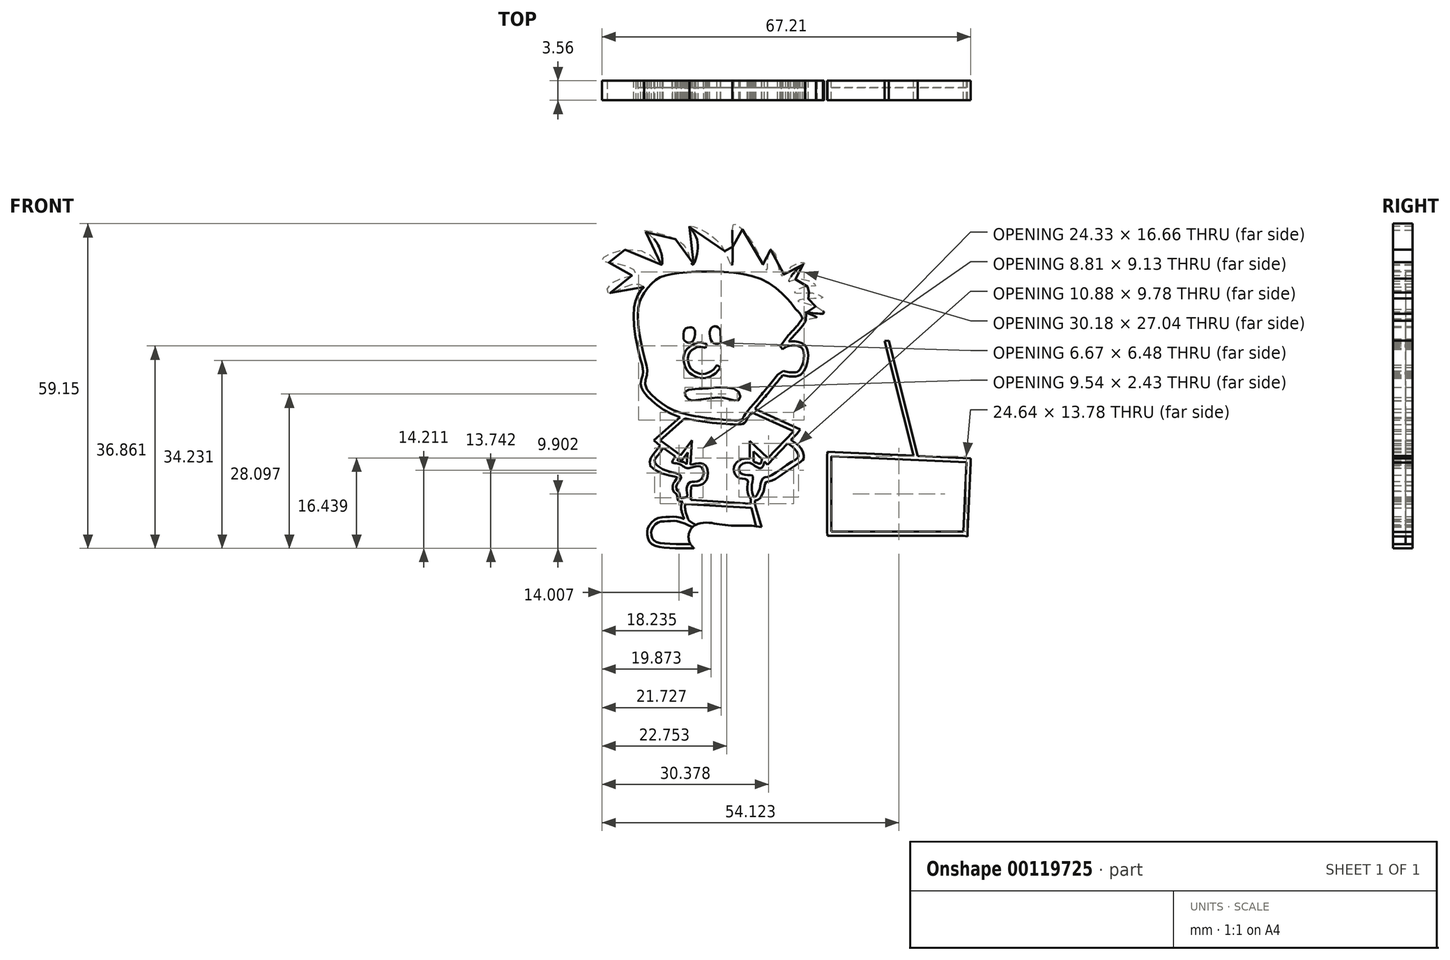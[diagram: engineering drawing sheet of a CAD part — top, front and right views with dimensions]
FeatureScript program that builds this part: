
annotation { "Feature Type Name" : "Feature", "Feature Type Description" : "" }
export const myFeature = defineFeature(function(context is Context, id is Id, definition is map)
    precondition{}
    {
        {
            var Q0;
            Q0=qCreatedBy(makeId("Front.planeOp"),FACE);
            var sketch = newSketch(context, id + "F0", { "sketchPlane" : qUnion([Q0])});
            skLineSegment(sketch, "E0.bottom", {"start": v(118.99, 18.23) * mm, "end": v(195.19, 18.23) * mm});
            skLineSegment(sketch, "E0.top", {"start": v(118.99, -45.27) * mm, "end": v(195.19, -45.27) * mm});
            skLineSegment(sketch, "E0.left", {"start": v(118.99, 18.23) * mm, "end": v(118.99, -45.27) * mm});
            skLineSegment(sketch, "E0.right", {"start": v(195.19, 18.23) * mm, "end": v(195.19, -45.27) * mm});
            skFitSpline(sketch, "E1", {"points": [v(128.75, 4.52) * mm, v(127.83, 2.6) * mm, v(127.76, -2.24) * mm, v(128.83, -7.5) * mm, v(129.18, -8.7) * mm, v(129.25, -10.42) * mm, v(128.9, -12.2) * mm, v(130.67, -14.61) * mm, v(133.8, -16.74) * mm, v(139.35, -18.17) * mm, v(146.53, -18.6) * mm, v(146.74, -18.24) * mm, v(148.73, -15.68) * mm, v(153.07, -10.42) * mm], "startDerivative": vector(-17.26, -27.17) * mm, "endDerivative": vector(40.4, 49.7) * mm});
            skFitSpline(sketch, "E2", {"points": [v(153.92, -10.49) * mm, v(156.84, -10.63) * mm, v(158.05, -9.35) * mm, v(158.62, -7.29) * mm, v(157.9, -4.94) * mm, v(155.06, -4.37) * mm, v(153.5, -5.15) * mm], "startDerivative": vector(17.4, -3.35) * mm, "endDerivative": vector(-9.1, -6.67) * mm});
            skFitSpline(sketch, "E3", {"points": [v(128.75, 5.58) * mm, v(126.4, 6) * mm, v(122.14, 4.52) * mm, v(122.92, 6.36) * mm, v(127.19, 8.07) * mm, v(125.2, 9.5) * mm, v(121.07, 10.42) * mm, v(122.78, 11.77) * mm, v(129.47, 11.63) * mm, v(131.88, 9.64) * mm, v(130.96, 13.76) * mm, v(128.75, 15.82) * mm, v(132.52, 15.04) * mm, v(136.58, 12.27) * mm, v(137.57, 9.64) * mm, v(138.35, 14.26) * mm, v(137, 16.6) * mm, v(142.12, 13.9) * mm, v(144.68, 9.5) * mm, v(144.82, 13.83) * mm, v(145.18, 17.1) * mm, v(147.45, 15.04) * mm, v(149.8, 11.06) * mm, v(151.15, 8.57) * mm, v(151.5, 12.2) * mm, v(152.5, 11.84) * mm, v(153.71, 7.64) * mm, v(155.92, 9.56) * mm, v(158.05, 10) * mm, v(157.05, 9.2) * mm, v(155.06, 6.65) * mm, v(157.05, 7.08) * mm, v(160.04, 5.87) * mm, v(157.76, 5.51) * mm, v(156.13, 4.52) * mm, v(159.12, 4.52) * mm, v(161.32, 3.6) * mm, v(158.55, 3.45) * mm, v(156.7, 3.02) * mm, v(159.47, 2.24) * mm, v(161.4, 0.75) * mm, v(158.2, 0.96) * mm, v(160.18, 0.04) * mm, v(159.4, -0.18) * mm, v(158.2, -0.6) * mm], "startDerivative": vector(-96.12, 50.27) * mm, "endDerivative": vector(-71.57, -34.9) * mm});
            skFitSpline(sketch, "E4", {"points": [v(155.06, -4.37) * mm, v(155.99, -3.3) * mm, v(157.27, -1.88) * mm, v(158.2, -0.6) * mm], "startDerivative": vector(2.8, 3.3) * mm, "endDerivative": vector(2.6, 3.86) * mm});
            skFitSpline(sketch, "E5", {"points": [v(137.88, -2.14) * mm, v(137.17, -1.78) * mm, v(136.15, -2.14) * mm, v(135.91, -3.15) * mm, v(135.97, -4) * mm, v(136.87, -4.6) * mm, v(137.64, -4.23) * mm, v(138.02, -2.92) * mm, v(137.88, -2.14) * mm]});
            skFitSpline(sketch, "E6", {"points": [v(142.49, -2.02) * mm, v(141.41, -1.6) * mm, v(140.75, -2.26) * mm, v(140.75, -3.63) * mm, v(141.35, -4.65) * mm, v(142.55, -4.59) * mm, v(142.67, -3.33) * mm, v(142.49, -2.02) * mm]});
            skFitSpline(sketch, "E7", {"points": [v(139.92, -5.55) * mm, v(138.9, -5.3) * mm, v(138.02, -5.57) * mm, v(136.8, -6.74) * mm, v(137.1, -9.07) * mm, v(138.02, -9.85) * mm, v(139.26, -10.27) * mm, v(140.93, -9.8) * mm, v(142.01, -8.66) * mm], "startDerivative": vector(-9.98, 3.85) * mm, "endDerivative": vector(7.15, 9.6) * mm});
            skLineSegment(sketch, "E8", {"start": v(136.3, -18.24) * mm, "end": v(131.64, -22.37) * mm});
            skLineSegment(sketch, "E9", {"start": v(148.14, -17.16) * mm, "end": v(155.97, -20.7) * mm});
            skLineSegment(sketch, "E10", {"start": v(155.97, -20.7) * mm, "end": v(150.65, -26.25) * mm});
            skLineSegment(sketch, "E11", {"start": v(150.65, -26.25) * mm, "end": v(148.7, -24.38) * mm});
            skLineSegment(sketch, "E12", {"start": v(148.7, -24.38) * mm, "end": v(148.7, -26.85) * mm});
            skFitSpline(sketch, "E13", {"points": [v(132.03, -24) * mm, v(131.28, -25.06) * mm, v(130.62, -26.17) * mm, v(131.83, -27.47) * mm, v(133.8, -28.18) * mm, v(135.4, -28.83) * mm, v(135.15, -29.79) * mm, v(134.54, -30.9) * mm, v(134.85, -31.6) * mm, v(134.95, -31.6) * mm], "startDerivative": vector(-5.75, -8.92) * mm, "endDerivative": vector(2.74, 1.08) * mm});
            skFitSpline(sketch, "E14", {"points": [v(136.05, -32.8) * mm, v(136.56, -32.6) * mm, v(136.5, -31.6) * mm, v(136.6, -30.7) * mm, v(137.1, -29.99) * mm, v(138.32, -29.89) * mm, v(139.42, -28.98) * mm, v(139.37, -27.52) * mm, v(138.57, -27.07) * mm, v(136.86, -27.42) * mm, v(136.05, -27.22) * mm, v(134.95, -26.62) * mm, v(133.84, -26.37) * mm, v(134.34, -25.41) * mm, v(134.44, -25.06) * mm], "startDerivative": vector(12.12, 1.45) * mm, "endDerivative": vector(0.3, 6.69) * mm});
            skFitSpline(sketch, "E15", {"points": [v(136.05, -32.8) * mm, v(135.35, -32.8) * mm, v(135.2, -32.2) * mm, v(134.95, -31.6) * mm], "startDerivative": vector(-2.5, -0.51) * mm, "endDerivative": vector(-0.94, 1.68) * mm});
            skLineSegment(sketch, "E16", {"start": v(131.64, -22.37) * mm, "end": v(135.42, -25.1) * mm});
            skLineSegment(sketch, "E17", {"start": v(135.42, -25.1) * mm, "end": v(137.4, -22.33) * mm});
            skLineSegment(sketch, "E18", {"start": v(137.4, -22.33) * mm, "end": v(137.14, -27.38) * mm});
            skPoint(sketch, "E19.1.internal.snap0", {"position": v(153.3, -23.47) * mm});
            skFitSpline(sketch, "E19", {"points": [v(154.73, -22.86) * mm, v(155.69, -23.47) * mm, v(156.6, -24.51) * mm, v(156.86, -25.31) * mm, v(155.48, -26.38) * mm, v(151.37, -28.99) * mm, v(150.41, -29.26) * mm, v(149.94, -30.43) * mm, v(149.72, -31.39) * mm, v(148.92, -32.72) * mm, v(148.44, -32.08) * mm, v(148.4, -30.32) * mm, v(148.5, -28.83) * mm, v(147.22, -28.67) * mm, v(146.05, -28.03) * mm, v(146.31, -26.91) * mm, v(147.75, -26.43) * mm, v(148.7, -26.85) * mm], "startDerivative": vector(18.4, -9.84) * mm, "endDerivative": vector(16.58, -11.15) * mm});
            skFitSpline(sketch, "E20", {"points": [v(148.7, -26.85) * mm, v(150.04, -27.44) * mm, v(150.65, -26.25) * mm], "startDerivative": vector(3, -2.09) * mm, "endDerivative": vector(0.9, 3.33) * mm});
            skFitSpline(sketch, "E21", {"points": [v(137.1, -37.14) * mm, v(134.8, -36.34) * mm, v(133, -36.34) * mm, v(130.92, -36.66) * mm, v(129.53, -38.1) * mm, v(129.27, -39.43) * mm, v(129.9, -41.08) * mm, v(132.04, -41.88) * mm, v(136.56, -42.04) * mm], "startDerivative": vector(-18.13, 7.82) * mm, "endDerivative": vector(27.1, 0) * mm});
            skFitSpline(sketch, "E22", {"points": [v(145.83, -37.94) * mm, v(142.8, -37.73) * mm, v(140.32, -37.37) * mm, v(137.9, -37.88) * mm, v(136.88, -39.38) * mm, v(137, -40.87) * mm, v(138.16, -42.3) * mm, v(141.04, -43.58) * mm, v(144.05, -43.85) * mm, v(147.49, -43.8) * mm, v(151.59, -43.8) * mm, v(153.3, -43.32) * mm, v(154.4, -41.88) * mm, v(154.1, -40.5) * mm, v(153.02, -39.06) * mm, v(151.53, -38.42) * mm, v(149.62, -38.1) * mm, v(147.97, -37.9) * mm, v(145.83, -37.94) * mm]});
            skFitSpline(sketch, "E23", {"points": [v(136.56, -42.04) * mm, v(137.84, -42.04) * mm], "startDerivative": vector(1.28, 0) * mm, "endDerivative": vector(1.28, 0) * mm});
            skFitSpline(sketch, "E24", {"points": [v(137.1, -37.14) * mm, v(137.52, -37.41) * mm, v(138.1, -37.77) * mm], "startDerivative": vector(0.86, -0.58) * mm, "endDerivative": vector(1.12, -0.67) * mm});
            skLineSegment(sketch, "E25", {"start": v(187.5, -26.36) * mm, "end": v(162.86, -25.25) * mm});
            skLineSegment(sketch, "E26", {"start": v(162.86, -25.25) * mm, "end": v(162.86, -39.03) * mm});
            skLineSegment(sketch, "E27", {"start": v(162.86, -39.03) * mm, "end": v(186.89, -39.03) * mm});
            skLineSegment(sketch, "E28", {"start": v(186.89, -39.03) * mm, "end": v(187.5, -26.36) * mm});
            skLineSegment(sketch, "E29", {"start": v(178.75, -25.82) * mm, "end": v(173.3, -4.2) * mm});
            skLineSegment(sketch, "E30", {"start": v(177.9, -25.59) * mm, "end": v(172.52, -4.23) * mm});
            skLineSegment(sketch, "E31", {"start": v(172.52, -4.23) * mm, "end": v(173.3, -4.2) * mm});
            skLineSegment(sketch, "E32", {"start": v(177.9, -25.59) * mm, "end": v(178, -25.93) * mm});
            skLineSegment(sketch, "E33", {"start": v(178.75, -25.82) * mm, "end": v(178.8, -25.97) * mm});
            skLineSegment(sketch, "E34.0", {"start": v(162.1, -25.25) * mm, "end": v(162.1, -39.03) * mm});
            skLineSegment(sketch, "E35.0", {"start": v(187.53, -25.6) * mm, "end": v(162.89, -24.49) * mm});
            skLineSegment(sketch, "E36.0", {"start": v(187.65, -39.06) * mm, "end": v(188.25, -26.4) * mm});
            skLineSegment(sketch, "E37.0", {"start": v(162.86, -39.79) * mm, "end": v(186.89, -39.79) * mm});
            skLineSegment(sketch, "E38", {"start": v(162.86, -39.79) * mm, "end": v(162.13, -39.79) * mm});
            skLineSegment(sketch, "E39", {"start": v(162.13, -39.79) * mm, "end": v(162.1, -39.03) * mm});
            skLineSegment(sketch, "E40", {"start": v(162.89, -24.49) * mm, "end": v(162.13, -24.45) * mm});
            skLineSegment(sketch, "E41", {"start": v(162.13, -24.45) * mm, "end": v(162.1, -25.25) * mm});
            skLineSegment(sketch, "E42", {"start": v(187.53, -25.6) * mm, "end": v(188.26, -25.63) * mm});
            skLineSegment(sketch, "E43", {"start": v(188.26, -25.63) * mm, "end": v(188.25, -26.4) * mm});
            skFitSpline(sketch, "E44", {"points": [v(136.36, -33.2) * mm, v(135.94, -33.42) * mm, v(135.67, -33.7) * mm, v(135.47, -34.19) * mm, v(135.46, -34.8) * mm, v(135.65, -35.6) * mm, v(135.87, -36.25) * mm, v(136.04, -36.7) * mm], "startDerivative": vector(-3.4, -1.64) * mm, "endDerivative": vector(1.3, -3.3) * mm});
            skLineSegment(sketch, "E45", {"start": v(148.92, -32.72) * mm, "end": v(148.92, -33.98) * mm});
            skLineSegment(sketch, "E46", {"start": v(148.92, -33.98) * mm, "end": v(136.36, -33.2) * mm});
            skFitSpline(sketch, "E47", {"points": [v(148.92, -33.98) * mm, v(150.1, -38.17) * mm], "startDerivative": vector(1.18, -4.2) * mm, "endDerivative": vector(1.18, -4.2) * mm});
            skLineSegment(sketch, "E48", {"start": v(136.56, -32.6) * mm, "end": v(136.56, -33.2) * mm});
            skLineSegment(sketch, "E49", {"start": v(187.65, -39.06) * mm, "end": v(187.65, -39.86) * mm});
            skLineSegment(sketch, "E50", {"start": v(187.65, -39.86) * mm, "end": v(186.89, -39.79) * mm});
            skLineSegment(sketch, "E51", {"start": v(132.03, -24) * mm, "end": v(132.67, -23.11) * mm});
            skLineSegment(sketch, "E52", {"start": v(132.67, -23.11) * mm, "end": v(132.74, -23.2) * mm});
            skLineSegment(sketch, "E53", {"start": v(134.44, -25.06) * mm, "end": v(134.76, -24.62) * mm});
            skLineSegment(sketch, "E54", {"start": v(134.76, -24.62) * mm, "end": v(134.66, -24.52) * mm});
            skLineSegment(sketch, "E55", {"start": v(136.3, -18.24) * mm, "end": v(136.87, -17.73) * mm});
            skLineSegment(sketch, "E56", {"start": v(148.14, -17.16) * mm, "end": v(147.66, -16.95) * mm});
            skLineSegment(sketch, "E57", {"start": v(154.73, -22.86) * mm, "end": v(154.2, -22.53) * mm});
            skLineSegment(sketch, "E58", {"start": v(128.75, 4.52) * mm, "end": v(128.75, 5.58) * mm});
            skFitSpline(sketch, "E59.0", {"points": [v(128.11, 4.92) * mm, v(127.93, 4.64) * mm, v(127.64, 4.18) * mm, v(127.3, 3.43) * mm, v(127.08, 2.78) * mm, v(126.93, 2.05) * mm, v(126.82, 1) * mm, v(126.81, -0.46) * mm, v(126.98, -2.38) * mm, v(127.3, -4.38) * mm, v(127.63, -5.91) * mm, v(127.88, -6.95) * mm, v(128.03, -7.5) * mm, v(128.14, -7.86) * mm, v(128.23, -8.17) * mm, v(128.33, -8.47) * mm, v(128.4, -8.73) * mm, v(128.45, -8.95) * mm, v(128.5, -9.2) * mm, v(128.54, -9.47) * mm, v(128.55, -9.75) * mm, v(128.54, -9.95) * mm, v(128.53, -10.15) * mm, v(128.5, -10.33) * mm, v(128.44, -10.53) * mm, v(128.35, -10.83) * mm, v(128.23, -11.17) * mm, v(128.14, -11.59) * mm, v(128.12, -11.88) * mm, v(128.12, -12.12) * mm, v(128.14, -12.31) * mm, v(128.18, -12.5) * mm, v(128.25, -12.75) * mm, v(128.37, -13.04) * mm, v(128.6, -13.47) * mm, v(128.97, -13.98) * mm, v(129.5, -14.55) * mm, v(130.05, -15.08) * mm, v(130.62, -15.58) * mm, v(131.21, -16.05) * mm, v(132.03, -16.64) * mm, v(133.12, -17.3) * mm, v(134.56, -17.92) * mm, v(135.92, -18.3) * mm, v(137.15, -18.58) * mm, v(138.15, -18.76) * mm, v(139.25, -18.92) * mm, v(140.45, -19.09) * mm, v(141.7, -19.23) * mm, v(142.95, -19.35) * mm, v(143.92, -19.42) * mm, v(144.63, -19.46) * mm, v(145.13, -19.47) * mm, v(145.58, -19.47) * mm, v(145.98, -19.46) * mm, v(146.27, -19.43) * mm, v(146.5, -19.4) * mm, v(146.65, -19.36) * mm, v(146.83, -19.3) * mm, v(147.03, -19.2) * mm, v(147.21, -19.03) * mm, v(147.34, -18.83) * mm, v(147.4, -18.68) * mm, v(147.43, -18.59) * mm, v(147.44, -18.54) * mm, v(147.45, -18.52) * mm, v(147.45, -18.51) * mm, v(147.46, -18.5) * mm, v(147.48, -18.45) * mm, v(147.52, -18.39) * mm, v(147.59, -18.28) * mm, v(147.7, -18.12) * mm, v(147.87, -17.9) * mm, v(148.07, -17.65) * mm, v(148.37, -17.28) * mm, v(148.8, -16.78) * mm, v(149.37, -16.11) * mm, v(149.95, -15.42) * mm, v(150.55, -14.7) * mm, v(151.36, -13.72) * mm, v(152.4, -12.45) * mm, v(153.24, -11.41) * mm, v(153.66, -10.9) * mm]});
            skFitSpline(sketch, "E60", {"points": [v(153.07, -10.42) * mm, v(153.36, -10.48) * mm, v(153.59, -10.5) * mm, v(153.92, -10.49) * mm], "startDerivative": vector(0.88, -0.23) * mm, "endDerivative": vector(0.98, 0.06) * mm});
            skFitSpline(sketch, "E61", {"points": [v(153.66, -10.9) * mm, v(153.92, -10.49) * mm], "startDerivative": vector(0.26, 0.4) * mm, "endDerivative": vector(0.26, 0.4) * mm});
            skFitSpline(sketch, "E62", {"points": [v(128.11, 4.92) * mm, v(128.75, 5.58) * mm], "startDerivative": vector(0.64, 0.66) * mm, "endDerivative": vector(0.64, 0.66) * mm});
            skFitSpline(sketch, "E63", {"points": [v(128.75, 4.52) * mm, v(130.9, 6.9) * mm, v(134.35, 8.04) * mm, v(141.92, 8.36) * mm, v(150.63, 6.74) * mm, v(155.23, 2.97) * mm, v(156.33, 1.55) * mm], "startDerivative": vector(14.38, 19.77) * mm, "endDerivative": vector(8.83, -12.25) * mm});
            skFitSpline(sketch, "E64.0", {"points": [v(154.48, -3.88) * mm, v(154.6, -3.74) * mm, v(154.83, -3.46) * mm, v(155.21, -3.02) * mm, v(155.65, -2.55) * mm, v(156.1, -2.06) * mm, v(156.54, -1.57) * mm, v(156.9, -1.11) * mm, v(157.24, -0.65) * mm, v(157.45, -0.34) * mm, v(157.56, -0.18) * mm]});
            skFitSpline(sketch, "E65", {"points": [v(156.33, 1.55) * mm, v(157.18, 0.63) * mm, v(157.56, -0.18) * mm], "startDerivative": vector(1.76, -1.68) * mm, "endDerivative": vector(0.66, -1.77) * mm});
            skFitSpline(sketch, "E66.0", {"points": [v(140.2, -4.84) * mm, v(140.08, -4.8) * mm, v(139.84, -4.7) * mm, v(139.47, -4.6) * mm, v(139.07, -4.54) * mm, v(138.63, -4.55) * mm, v(138.23, -4.64) * mm, v(137.87, -4.79) * mm, v(137.53, -4.96) * mm, v(137.14, -5.2) * mm, v(136.73, -5.51) * mm, v(136.4, -5.88) * mm, v(136.2, -6.23) * mm, v(136.06, -6.54) * mm, v(135.98, -6.85) * mm, v(135.93, -7.27) * mm, v(135.93, -7.8) * mm, v(136.03, -8.4) * mm, v(136.2, -8.96) * mm, v(136.44, -9.47) * mm, v(136.76, -9.9) * mm, v(137.12, -10.21) * mm, v(137.4, -10.4) * mm, v(137.62, -10.5) * mm, v(137.82, -10.6) * mm, v(138.1, -10.75) * mm, v(138.5, -10.9) * mm, v(138.98, -11.02) * mm, v(139.5, -11.05) * mm, v(140.01, -10.98) * mm, v(140.51, -10.85) * mm, v(140.9, -10.69) * mm, v(141.2, -10.52) * mm, v(141.5, -10.34) * mm, v(141.81, -10.08) * mm, v(142.23, -9.64) * mm, v(142.47, -9.31) * mm, v(142.62, -9.11) * mm]});
            skLineSegment(sketch, "E67", {"start": v(139.92, -5.55) * mm, "end": v(140.2, -4.84) * mm});
            skLineSegment(sketch, "E68", {"start": v(142.01, -8.66) * mm, "end": v(142.62, -9.11) * mm});
            skFitSpline(sketch, "E69.0", {"points": [v(154.07, -9.74) * mm, v(154.43, -9.8) * mm, v(154.96, -9.9) * mm, v(155.59, -9.99) * mm, v(156, -10) * mm, v(156.29, -9.99) * mm, v(156.46, -9.95) * mm, v(156.57, -9.92) * mm, v(156.66, -9.88) * mm, v(156.78, -9.8) * mm, v(156.92, -9.69) * mm, v(157.1, -9.48) * mm, v(157.26, -9.22) * mm, v(157.42, -8.9) * mm, v(157.6, -8.48) * mm, v(157.74, -8.04) * mm, v(157.83, -7.56) * mm, v(157.88, -7.05) * mm, v(157.86, -6.51) * mm, v(157.75, -6.06) * mm, v(157.63, -5.78) * mm, v(157.5, -5.6) * mm, v(157.38, -5.49) * mm, v(157.22, -5.38) * mm, v(156.96, -5.25) * mm, v(156.58, -5.13) * mm, v(156.15, -5.07) * mm, v(155.72, -5.06) * mm, v(155.32, -5.1) * mm, v(155, -5.16) * mm, v(154.73, -5.27) * mm, v(154.4, -5.45) * mm, v(154.14, -5.63) * mm, v(153.95, -5.77) * mm]});
            skLineSegment(sketch, "E70", {"start": v(153.5, -5.15) * mm, "end": v(153.95, -5.77) * mm});
            skLineSegment(sketch, "E71", {"start": v(153.07, -10.42) * mm, "end": v(154.07, -9.74) * mm});
            skLineSegment(sketch, "E72", {"start": v(154.48, -3.88) * mm, "end": v(153.7, -5) * mm});
            skLineSegment(sketch, "E73.0", {"start": v(135.8, -17.67) * mm, "end": v(131.13, -21.8) * mm});
            skLineSegment(sketch, "E74.0", {"start": v(131.2, -22.98) * mm, "end": v(134.98, -25.71) * mm});
            skFitSpline(sketch, "E75", {"points": [v(131.62, -23.3) * mm, v(130.74, -24.45) * mm, v(129.94, -25.66) * mm, v(129.96, -27.19) * mm, v(134.04, -28.94) * mm, v(134.68, -29.07) * mm, v(134.6, -29.37) * mm, v(134.08, -30.17) * mm, v(133.91, -30.72) * mm, v(134.03, -31.53) * mm, v(134.33, -31.96) * mm, v(134.66, -32.2) * mm, v(134.76, -32.87) * mm, v(135.05, -33.43) * mm, v(135.81, -33.53) * mm], "startDerivative": vector(-10.04, -13.05) * mm, "endDerivative": vector(13.26, 0.4) * mm});
            skFitSpline(sketch, "E76", {"points": [v(137.23, -33.25) * mm, v(137.27, -31.33) * mm, v(137.46, -30.67) * mm, v(138.9, -30.54) * mm, v(140.18, -29.36) * mm, v(140.18, -27.4) * mm, v(139.3, -26.6) * mm, v(137.74, -26.7) * mm, v(136.63, -26.82) * mm, v(136, -26.37) * mm, v(134.83, -26) * mm, v(134.98, -25.71) * mm], "startDerivative": vector(0.42, 18.3) * mm, "endDerivative": vector(6.45, 6.8) * mm});
            skLineSegment(sketch, "E77", {"start": v(134.98, -25.71) * mm, "end": v(135.42, -25.1) * mm});
            skLineSegment(sketch, "E78", {"start": v(131.13, -21.8) * mm, "end": v(130.52, -22.33) * mm});
            skLineSegment(sketch, "E79", {"start": v(130.52, -22.33) * mm, "end": v(131.2, -22.98) * mm});
            skLineSegment(sketch, "E80", {"start": v(134.98, -25.71) * mm, "end": v(135.55, -26.12) * mm});
            skLineSegment(sketch, "E81", {"start": v(135.55, -26.12) * mm, "end": v(136.65, -24.6) * mm});
            skLineSegment(sketch, "E82", {"start": v(136.65, -24.6) * mm, "end": v(136.49, -26.74) * mm});
            skLineSegment(sketch, "E83.0", {"start": v(148.45, -16.47) * mm, "end": v(156.28, -20) * mm});
            skLineSegment(sketch, "E84.0", {"start": v(156.52, -21.22) * mm, "end": v(151.2, -26.78) * mm});
            skLineSegment(sketch, "E85", {"start": v(150.65, -26.25) * mm, "end": v(151.2, -26.78) * mm});
            skLineSegment(sketch, "E86", {"start": v(147.99, -26.48) * mm, "end": v(147.99, -23.15) * mm});
            skLineSegment(sketch, "E87", {"start": v(147.99, -23.15) * mm, "end": v(147.99, -22.48) * mm});
            skLineSegment(sketch, "E88", {"start": v(147.99, -22.48) * mm, "end": v(151.26, -25.61) * mm});
            skLineSegment(sketch, "E89", {"start": v(156.28, -20) * mm, "end": v(157.2, -20.4) * mm});
            skLineSegment(sketch, "E90", {"start": v(157.2, -20.4) * mm, "end": v(156.52, -21.22) * mm});
            skFitSpline(sketch, "E91", {"points": [v(150.2, -25.82) * mm, v(149.96, -26.6) * mm, v(149.75, -26.63) * mm, v(148.7, -26.25) * mm], "startDerivative": vector(-0.55, -2.67) * mm, "endDerivative": vector(-2.86, 1.13) * mm});
            skFitSpline(sketch, "E92", {"points": [v(147.99, -25.73) * mm, v(146.49, -25.8) * mm, v(145.3, -26.76) * mm, v(145.12, -28.02) * mm, v(145.96, -29.22) * mm, v(147.52, -29.57) * mm, v(147.54, -30.56) * mm, v(147.63, -31.99) * mm, v(148.17, -33.05) * mm, v(148.92, -33.35) * mm, v(149.83, -32.94) * mm, v(150.63, -31.15) * mm, v(150.91, -30) * mm, v(151.73, -29.8) * mm, v(154.25, -28.3) * mm, v(157.55, -26.04) * mm, v(157.85, -25.47) * mm, v(157.43, -23.98) * mm, v(155.47, -22.31) * mm], "startDerivative": vector(-27.5, 2.83) * mm, "endDerivative": vector(-31.68, 20.73) * mm});
            skLineSegment(sketch, "E93", {"start": v(148.17, -33.05) * mm, "end": v(148.17, -33.93) * mm});
            skLineSegment(sketch, "E94.0", {"start": v(148.88, -34.74) * mm, "end": v(136.3, -33.95) * mm});
            skFitSpline(sketch, "E95.0", {"points": [v(146.53, -38.7) * mm, v(145.85, -38.7) * mm, v(145.1, -38.7) * mm, v(144.33, -38.66) * mm, v(143.55, -38.6) * mm, v(142.92, -38.52) * mm, v(142.44, -38.44) * mm, v(141.98, -38.36) * mm, v(141.44, -38.26) * mm, v(140.84, -38.17) * mm, v(140.26, -38.12) * mm, v(139.64, -38.13) * mm, v(139.05, -38.22) * mm, v(138.64, -38.35) * mm, v(138.37, -38.48) * mm, v(138.16, -38.63) * mm, v(137.93, -38.87) * mm, v(137.72, -39.22) * mm, v(137.6, -39.6) * mm, v(137.57, -39.96) * mm, v(137.6, -40.31) * mm, v(137.75, -40.77) * mm, v(138.06, -41.23) * mm, v(138.58, -41.68) * mm, v(139.26, -42.13) * mm, v(140.12, -42.52) * mm, v(141.03, -42.8) * mm, v(141.7, -42.95) * mm, v(142.37, -43.04) * mm, v(143.27, -43.1) * mm, v(144.45, -43.09) * mm, v(145.69, -43.06) * mm, v(146.76, -43.04) * mm, v(147.62, -43.03) * mm, v(148.53, -43.05) * mm, v(149.44, -43.06) * mm, v(150.31, -43.07) * mm, v(151.1, -43.06) * mm, v(151.77, -43.03) * mm, v(152.25, -42.96) * mm, v(152.54, -42.87) * mm, v(152.75, -42.76) * mm, v(152.92, -42.65) * mm, v(153.1, -42.51) * mm, v(153.27, -42.35) * mm, v(153.42, -42.18) * mm, v(153.54, -42) * mm, v(153.63, -41.84) * mm, v(153.66, -41.73) * mm, v(153.67, -41.67) * mm, v(153.68, -41.6) * mm, v(153.68, -41.52) * mm, v(153.65, -41.39) * mm, v(153.6, -41.22) * mm, v(153.5, -41.03) * mm, v(153.4, -40.8) * mm, v(153.27, -40.57) * mm, v(153.1, -40.28) * mm, v(152.9, -40.02) * mm, v(152.71, -39.8) * mm, v(152.57, -39.66) * mm, v(152.43, -39.56) * mm, v(152.21, -39.43) * mm, v(151.9, -39.3) * mm, v(151.44, -39.17) * mm, v(150.9, -39.06) * mm, v(150.34, -38.97) * mm, v(149.76, -38.89) * mm, v(149.2, -38.8) * mm, v(148.68, -38.73) * mm, v(148.2, -38.68) * mm, v(147.7, -38.66) * mm, v(147.15, -38.67) * mm, v(146.53, -38.7) * mm, v(145.85, -38.7) * mm, v(145.1, -38.7) * mm, v(146.53, -38.7) * mm]});
            skFitSpline(sketch, "E96.0", {"points": [v(136.8, -37.84) * mm, v(136.43, -37.68) * mm, v(135.88, -37.44) * mm, v(135.21, -37.2) * mm, v(134.83, -37.11) * mm, v(134.56, -37.07) * mm, v(134.3, -37.05) * mm, v(133.94, -37.05) * mm, v(133.55, -37.07) * mm, v(133.2, -37.1) * mm, v(132.93, -37.1) * mm, v(132.66, -37.12) * mm, v(132.3, -37.13) * mm, v(131.9, -37.16) * mm, v(131.55, -37.23) * mm, v(131.32, -37.31) * mm, v(131.1, -37.41) * mm, v(130.84, -37.61) * mm, v(130.54, -37.92) * mm, v(130.34, -38.21) * mm, v(130.21, -38.44) * mm, v(130.12, -38.65) * mm, v(130.05, -38.87) * mm, v(130.02, -39.1) * mm, v(130.02, -39.32) * mm, v(130.04, -39.56) * mm, v(130.1, -39.89) * mm, v(130.24, -40.25) * mm, v(130.39, -40.48) * mm, v(130.51, -40.61) * mm, v(130.66, -40.73) * mm, v(130.93, -40.87) * mm, v(131.38, -41) * mm, v(131.94, -41.1) * mm, v(132.6, -41.18) * mm, v(133.55, -41.24) * mm, v(134.87, -41.28) * mm, v(136, -41.28) * mm, v(136.56, -41.28) * mm]});
            skLineSegment(sketch, "E97", {"start": v(136.56, -41.28) * mm, "end": v(137.2, -41.28) * mm});
            skLineSegment(sketch, "E98", {"start": v(137.2, -41.28) * mm, "end": v(137.2, -41.33) * mm});
            skLineSegment(sketch, "E99", {"start": v(136.82, -37.83) * mm, "end": v(137.53, -38.19) * mm});
            skFitSpline(sketch, "E100", {"points": [v(136.3, -33.95) * mm, v(136.22, -34.12) * mm, v(136.17, -34.46) * mm, v(136.3, -35.45) * mm, v(136.9, -37.05) * mm], "startDerivative": vector(-0.76, -1.18) * mm, "endDerivative": vector(1.78, -4.2) * mm});
            skFitSpline(sketch, "E101", {"points": [v(148.88, -34.74) * mm, v(149.14, -34.74) * mm], "startDerivative": vector(0.26, 0) * mm, "endDerivative": vector(0.26, 0) * mm});
            skFitSpline(sketch, "E102", {"points": [v(148.27, -34.7) * mm, v(149.14, -38.03) * mm], "startDerivative": vector(0.86, -3.34) * mm, "endDerivative": vector(0.86, -3.34) * mm});
            skFitSpline(sketch, "E103", {"points": [v(136.15, -13.53) * mm, v(139.2, -12.96) * mm, v(142.42, -12.72) * mm, v(145.98, -13.53) * mm, v(145.9, -15.07) * mm, v(143.56, -14.66) * mm, v(140.57, -14.74) * mm, v(138.02, -15.07) * mm, v(136.8, -14.9) * mm, v(136.15, -13.53) * mm]});
            skLineSegment(sketch, "E104", {"start": v(136.82, -37.83) * mm, "end": v(136.8, -37.84) * mm});
            skSolve(sketch);
        }
        {
            var Q0;
            Q0=makeQuery(id+"F0.imprint","IMPRINT",FACE,{"disambiguationData":[TD([[makeQuery(id+"F0.imprint","IMPRINT",EDGE,{"derivedFrom":sQuery(id+"F0.wireOp",EDGE,"E5")}),-1.0]])]});
            var Q1;
            {var subQ0=sQuery(id+"F0.wireOp",EDGE,"E17");Q1=makeQuery(id+"F0.imprint","IMPRINT",FACE,{"disambiguationData":[TD([[makeQuery(id+"F0.imprint","IMPRINT",EDGE,{"derivedFrom":subQ0}),1.0]])]});}
            var Q2;
            {var subQ8=sQuery(id+"F0.wireOp",EDGE,"E13");Q2=makeQuery(id+"F0.imprint","IMPRINT",FACE,{"disambiguationData":[TD([[makeQuery(id+"F0.imprint","IMPRINT",EDGE,{"derivedFrom":subQ8}),1.0]])]});}
            var Q3;
            {var subQ0=sQuery(id+"F0.wireOp",EDGE,"E20");Q3=makeQuery(id+"F0.imprint","IMPRINT",FACE,{"disambiguationData":[TD([[makeQuery(id+"F0.imprint","IMPRINT",EDGE,{"derivedFrom":subQ0}),-1.0]])]});}
            var Q4;
            {var subQ0=sQuery(id+"F0.wireOp",EDGE,"E24");Q4=makeQuery(id+"F0.imprint","IMPRINT",FACE,{"disambiguationData":[TD([[makeQuery(id+"F0.imprint","IMPRINT",EDGE,{"derivedFrom":subQ0}),1.0]])]});}
            var Q5;
            Q5=makeQuery(id+"F0.imprint","IMPRINT",FACE,{"disambiguationData":[TD([[makeQuery(id+"F0.imprint","IMPRINT",EDGE,{"derivedFrom":sQuery(id+"F0.wireOp",EDGE,"E95.0")}),1.0]])]});
            var Q6;
            Q6=makeQuery(id+"F0.imprint","IMPRINT",FACE,{"disambiguationData":[TD([[makeQuery(id+"F0.imprint","IMPRINT",EDGE,{"derivedFrom":sQuery(id+"F0.wireOp",EDGE,"E96.0")}),1.0]])]});
            var Q7;
            {var subQ0=sQuery(id+"F0.wireOp",EDGE,"E26");Q7=makeQuery(id+"F0.imprint","IMPRINT",FACE,{"disambiguationData":[TD([[makeQuery(id+"F0.imprint","IMPRINT",EDGE,{"derivedFrom":subQ0}),1.0]])]});}
            extrude(context, id + "F1", {"entities" : qUnion([Q0, Q1, Q2, Q3, Q4, Q5, Q6, Q7]), "depth" : 1.27 * mm});
        }
        {
            var Q0;
            Q0=makeQuery(id+"F0.imprint","IMPRINT",FACE,{"disambiguationData":[TD([[makeQuery(id+"F0.imprint","IMPRINT",EDGE,{"derivedFrom":sQuery(id+"F0.wireOp",EDGE,"E3")}),-1.0]])]});
            var Q1;
            {var subQ2=sQuery(id+"F0.wireOp",EDGE,"E55");Q1=makeQuery(id+"F0.imprint","IMPRINT",FACE,{"disambiguationData":[TD([[makeQuery(id+"F0.imprint","IMPRINT",EDGE,{"derivedFrom":subQ2}),1.0]])]});}
            var Q2;
            {var subQ0=sQuery(id+"F0.wireOp",EDGE,"E60");Q2=makeQuery(id+"F0.imprint","IMPRINT",FACE,{"disambiguationData":[TD([[makeQuery(id+"F0.imprint","IMPRINT",EDGE,{"derivedFrom":subQ0}),1.0]])]});}
            var Q3;
            {var subQ0=sQuery(id+"F0.wireOp",EDGE,"E56");Q3=makeQuery(id+"F0.imprint","IMPRINT",FACE,{"disambiguationData":[TD([[makeQuery(id+"F0.imprint","IMPRINT",EDGE,{"derivedFrom":subQ0}),-1.0]])]});}
            var Q4;
            {var subQ0=sQuery(id+"F0.wireOp",EDGE,"E55");Q4=makeQuery(id+"F0.imprint","IMPRINT",FACE,{"disambiguationData":[TD([[makeQuery(id+"F0.imprint","IMPRINT",EDGE,{"derivedFrom":subQ0}),-1.0]])]});}
            var Q5;
            Q5=makeQuery(id+"F0.imprint","IMPRINT",FACE,{"disambiguationData":[TD([[makeQuery(id+"F0.imprint","IMPRINT",EDGE,{"derivedFrom":sQuery(id+"F0.wireOp",EDGE,"E103")}),-1.0]])]});
            var Q6;
            Q6=makeQuery(id+"F0.imprint","IMPRINT",FACE,{"disambiguationData":[TD([[makeQuery(id+"F0.imprint","IMPRINT",EDGE,{"derivedFrom":sQuery(id+"F0.wireOp",EDGE,"E7")}),-1.0]])]});
            var Q7;
            Q7=makeQuery(id+"F0.imprint","IMPRINT",FACE,{"disambiguationData":[TD([[makeQuery(id+"F0.imprint","IMPRINT",EDGE,{"derivedFrom":sQuery(id+"F0.wireOp",EDGE,"E5")}),1.0]])]});
            var Q8;
            Q8=makeQuery(id+"F0.imprint","IMPRINT",FACE,{"disambiguationData":[TD([[makeQuery(id+"F0.imprint","IMPRINT",EDGE,{"derivedFrom":sQuery(id+"F0.wireOp",EDGE,"E6")}),1.0]])]});
            var Q9;
            {var subQ0=sQuery(id+"F0.wireOp",EDGE,"E57");Q9=makeQuery(id+"F0.imprint","IMPRINT",FACE,{"disambiguationData":[TD([[makeQuery(id+"F0.imprint","IMPRINT",EDGE,{"derivedFrom":subQ0}),-1.0]])]});}
            var Q10;
            {var subQ12=sQuery(id+"F0.wireOp",EDGE,"E78");Q10=makeQuery(id+"F0.imprint","IMPRINT",FACE,{"disambiguationData":[TD([[makeQuery(id+"F0.imprint","IMPRINT",EDGE,{"derivedFrom":subQ12}),1.0]])]});}
            var Q11;
            {var subQ0=sQuery(id+"F0.wireOp",EDGE,"E53");Q11=makeQuery(id+"F0.imprint","IMPRINT",FACE,{"disambiguationData":[TD([[makeQuery(id+"F0.imprint","IMPRINT",EDGE,{"derivedFrom":subQ0}),1.0]])]});}
            var Q12;
            {var subQ5=sQuery(id+"F0.wireOp",EDGE,"E53");Q12=makeQuery(id+"F0.imprint","IMPRINT",FACE,{"disambiguationData":[TD([[makeQuery(id+"F0.imprint","IMPRINT",EDGE,{"derivedFrom":subQ5}),-1.0]])]});}
            var Q13;
            {var subQ4=sQuery(id+"F0.wireOp",EDGE,"E17");Q13=makeQuery(id+"F0.imprint","IMPRINT",FACE,{"disambiguationData":[TD([[makeQuery(id+"F0.imprint","IMPRINT",EDGE,{"derivedFrom":subQ4}),-1.0]])]});}
            var Q14;
            {var subQ0=sQuery(id+"F0.wireOp",EDGE,"E57");Q14=makeQuery(id+"F0.imprint","IMPRINT",FACE,{"disambiguationData":[TD([[makeQuery(id+"F0.imprint","IMPRINT",EDGE,{"derivedFrom":subQ0}),1.0]])]});}
            var Q15;
            {var subQ10=sQuery(id+"F0.wireOp",EDGE,"E87");Q15=makeQuery(id+"F0.imprint","IMPRINT",FACE,{"disambiguationData":[TD([[makeQuery(id+"F0.imprint","IMPRINT",EDGE,{"derivedFrom":subQ10}),-1.0]])]});}
            var Q16;
            {var subQ0=sQuery(id+"F0.wireOp",EDGE,"E20");Q16=makeQuery(id+"F0.imprint","IMPRINT",FACE,{"disambiguationData":[TD([[makeQuery(id+"F0.imprint","IMPRINT",EDGE,{"derivedFrom":subQ0}),1.0]])]});}
            var Q17;
            {var subQ4=sQuery(id+"F0.wireOp",EDGE,"E19");var subQ6=sQuery(id+"F0.wireOp",EDGE,"E45");var subQ7=makeQuery(id+"F0.imprint","INTERSECT",VERTEX,{"derivedFrom":[subQ4,subQ6]});Q17=makeQuery(id+"F0.imprint","IMPRINT",FACE,{"disambiguationData":[TD([[makeQuery(id+"F0.imprint","IMPRINT",EDGE,{"disambiguationData":[TD([[subQ7,-1.0]])],"derivedFrom":subQ4}),1.0]])]});}
            var Q18;
            {var subQ2=sQuery(id+"F0.wireOp",EDGE,"E18");var subQ4=sQuery(id+"F0.wireOp",EDGE,"E14");var subQ5=makeQuery(id+"F0.imprint","INTERSECT",VERTEX,{"derivedFrom":[subQ4,subQ2]});Q18=makeQuery(id+"F0.imprint","IMPRINT",FACE,{"disambiguationData":[TD([[makeQuery(id+"F0.imprint","IMPRINT",EDGE,{"disambiguationData":[TD([[subQ5,-1.0]])],"derivedFrom":subQ4}),-1.0]])]});}
            var Q19;
            {var subQ0=sQuery(id+"F0.wireOp",EDGE,"E48");Q19=makeQuery(id+"F0.imprint","IMPRINT",FACE,{"disambiguationData":[TD([[makeQuery(id+"F0.imprint","IMPRINT",EDGE,{"derivedFrom":subQ0}),1.0]])]});}
            var Q20;
            {var subQ0=sQuery(id+"F0.wireOp",EDGE,"E45");var subQ1=sQuery(id+"F0.wireOp",EDGE,"E19");var subQ2=makeQuery(id+"F0.imprint","INTERSECT",VERTEX,{"derivedFrom":[subQ1,subQ0]});Q20=makeQuery(id+"F0.imprint","IMPRINT",FACE,{"disambiguationData":[TD([[makeQuery(id+"F0.imprint","IMPRINT",EDGE,{"disambiguationData":[TD([[subQ2,1.0]])],"derivedFrom":subQ1}),1.0]])]});}
            var Q21;
            {var subQ7=sQuery(id+"F0.wireOp",EDGE,"E13");Q21=makeQuery(id+"F0.imprint","IMPRINT",FACE,{"disambiguationData":[TD([[makeQuery(id+"F0.imprint","IMPRINT",EDGE,{"derivedFrom":subQ7}),-1.0]])]});}
            var Q22;
            {var subQ3=sQuery(id+"F0.wireOp",EDGE,"E100");Q22=makeQuery(id+"F0.imprint","IMPRINT",FACE,{"disambiguationData":[TD([[makeQuery(id+"F0.imprint","IMPRINT",EDGE,{"derivedFrom":subQ3}),-1.0]])]});}
            var Q23;
            {var subQ0=sQuery(id+"F0.wireOp",EDGE,"E101");Q23=makeQuery(id+"F0.imprint","IMPRINT",FACE,{"disambiguationData":[TD([[makeQuery(id+"F0.imprint","IMPRINT",EDGE,{"derivedFrom":subQ0}),-1.0]])]});}
            var Q24;
            {var subQ5=sQuery(id+"F0.wireOp",EDGE,"E93");Q24=makeQuery(id+"F0.imprint","IMPRINT",FACE,{"disambiguationData":[TD([[makeQuery(id+"F0.imprint","IMPRINT",EDGE,{"derivedFrom":subQ5}),1.0]])]});}
            var Q25;
            Q25=makeQuery(id+"F0.imprint","IMPRINT",FACE,{"disambiguationData":[TD([[makeQuery(id+"F0.imprint","IMPRINT",EDGE,{"derivedFrom":sQuery(id+"F0.wireOp",EDGE,"E95.0")}),-1.0]])]});
            var Q26;
            {var subQ2=sQuery(id+"F0.wireOp",EDGE,"E23");Q26=makeQuery(id+"F0.imprint","IMPRINT",FACE,{"disambiguationData":[TD([[makeQuery(id+"F0.imprint","IMPRINT",EDGE,{"derivedFrom":subQ2}),1.0]])]});}
            var Q27;
            {var subQ9=sQuery(id+"F0.wireOp",EDGE,"E26");Q27=makeQuery(id+"F0.imprint","IMPRINT",FACE,{"disambiguationData":[TD([[makeQuery(id+"F0.imprint","IMPRINT",EDGE,{"derivedFrom":subQ9}),-1.0]])]});}
            var Q28;
            {var subQ0=sQuery(id+"F0.wireOp",EDGE,"E32");Q28=makeQuery(id+"F0.imprint","IMPRINT",FACE,{"disambiguationData":[TD([[makeQuery(id+"F0.imprint","IMPRINT",EDGE,{"derivedFrom":subQ0}),1.0]])]});}
            var Q29;
            {var subQ0=sQuery(id+"F0.wireOp",EDGE,"E31");Q29=makeQuery(id+"F0.imprint","IMPRINT",FACE,{"disambiguationData":[TD([[makeQuery(id+"F0.imprint","IMPRINT",EDGE,{"derivedFrom":subQ0}),-1.0]])]});}
            extrude(context, id + "F2", {"entities" : qUnion([Q0, Q1, Q2, Q3, Q4, Q5, Q6, Q7, Q8, Q9, Q10, Q11, Q12, Q13, Q14, Q15, Q16, Q17, Q18, Q19, Q20, Q21, Q22, Q23, Q24, Q25, Q26, Q27, Q28, Q29]), "depth" : 3.56 * mm});
        }
    });
